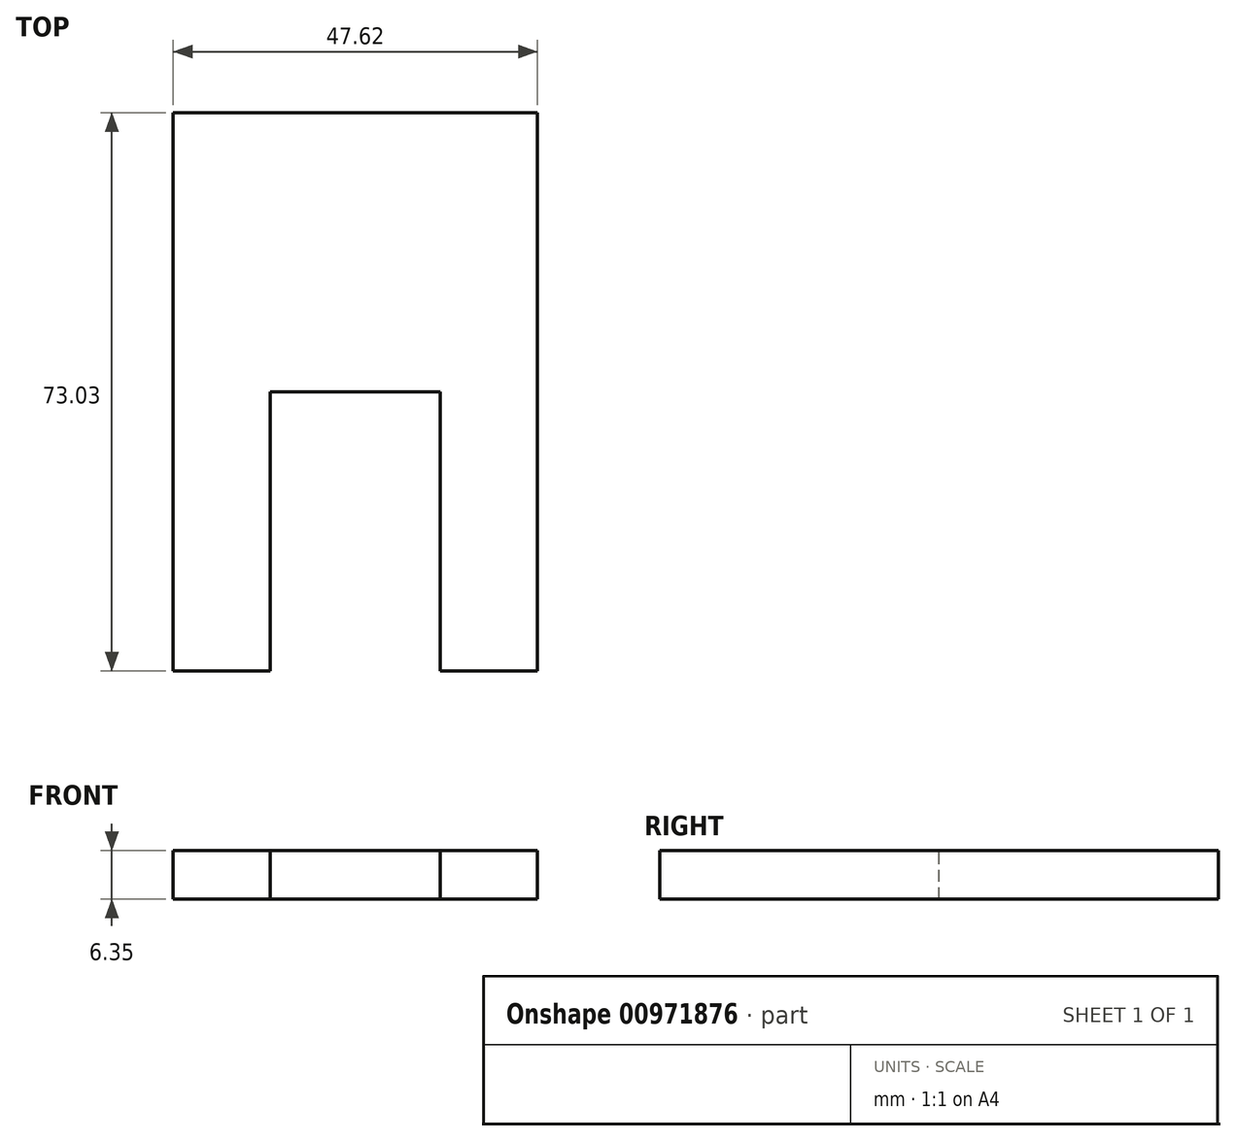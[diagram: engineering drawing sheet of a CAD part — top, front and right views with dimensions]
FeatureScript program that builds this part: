
annotation { "Feature Type Name" : "Feature", "Feature Type Description" : "" }
export const myFeature = defineFeature(function(context is Context, id is Id, definition is map)
    precondition{}
    {
        {
            var Q0;
            Q0=qCreatedBy(makeId("Top.planeOp"),FACE);
            var sketch = newSketch(context, id + "F0", { "sketchPlane" : qUnion([Q0])});
            skLineSegment(sketch, "E0.bottom", {"start": v(0, 0) * mm, "end": v(-12.7, 0) * mm});
            skLineSegment(sketch, "E0.top", {"start": v(0, 73.02) * mm, "end": v(-47.63, 73.02) * mm});
            skLineSegment(sketch, "E0.left", {"start": v(0, 0) * mm, "end": v(0, 73.02) * mm});
            skLineSegment(sketch, "E0.right", {"start": v(-47.63, 0) * mm, "end": v(-47.63, 73.02) * mm});
            skLineSegment(sketch, "E1.top", {"start": v(-12.7, 36.51) * mm, "end": v(-34.93, 36.51) * mm});
            skLineSegment(sketch, "E1.left", {"start": v(-12.7, 0) * mm, "end": v(-12.7, 36.51) * mm});
            skLineSegment(sketch, "E1.right", {"start": v(-34.92, 0) * mm, "end": v(-34.93, 36.51) * mm});
            skLineSegment(sketch, "E2.trimOffspring", {"start": v(-34.92, 0) * mm, "end": v(-47.62, 0) * mm});
            skSolve(sketch);
        }
        {
            var Q0;
            Q0=makeQuery(id+"F0.imprint","IMPRINT",FACE,{"disambiguationData":[TD([[makeQuery(id+"F0.imprint","IMPRINT",EDGE,{"derivedFrom":sQuery(id+"F0.wireOp",EDGE,"E0.bottom")}),-1.0]])]});
            extrude(context, id + "F1", {"entities" : qUnion([Q0]), "oppositeDirection" : true, "depth" : 6.35 * mm, "offsetDistance" : 25.4 * mm});
        }
    });
